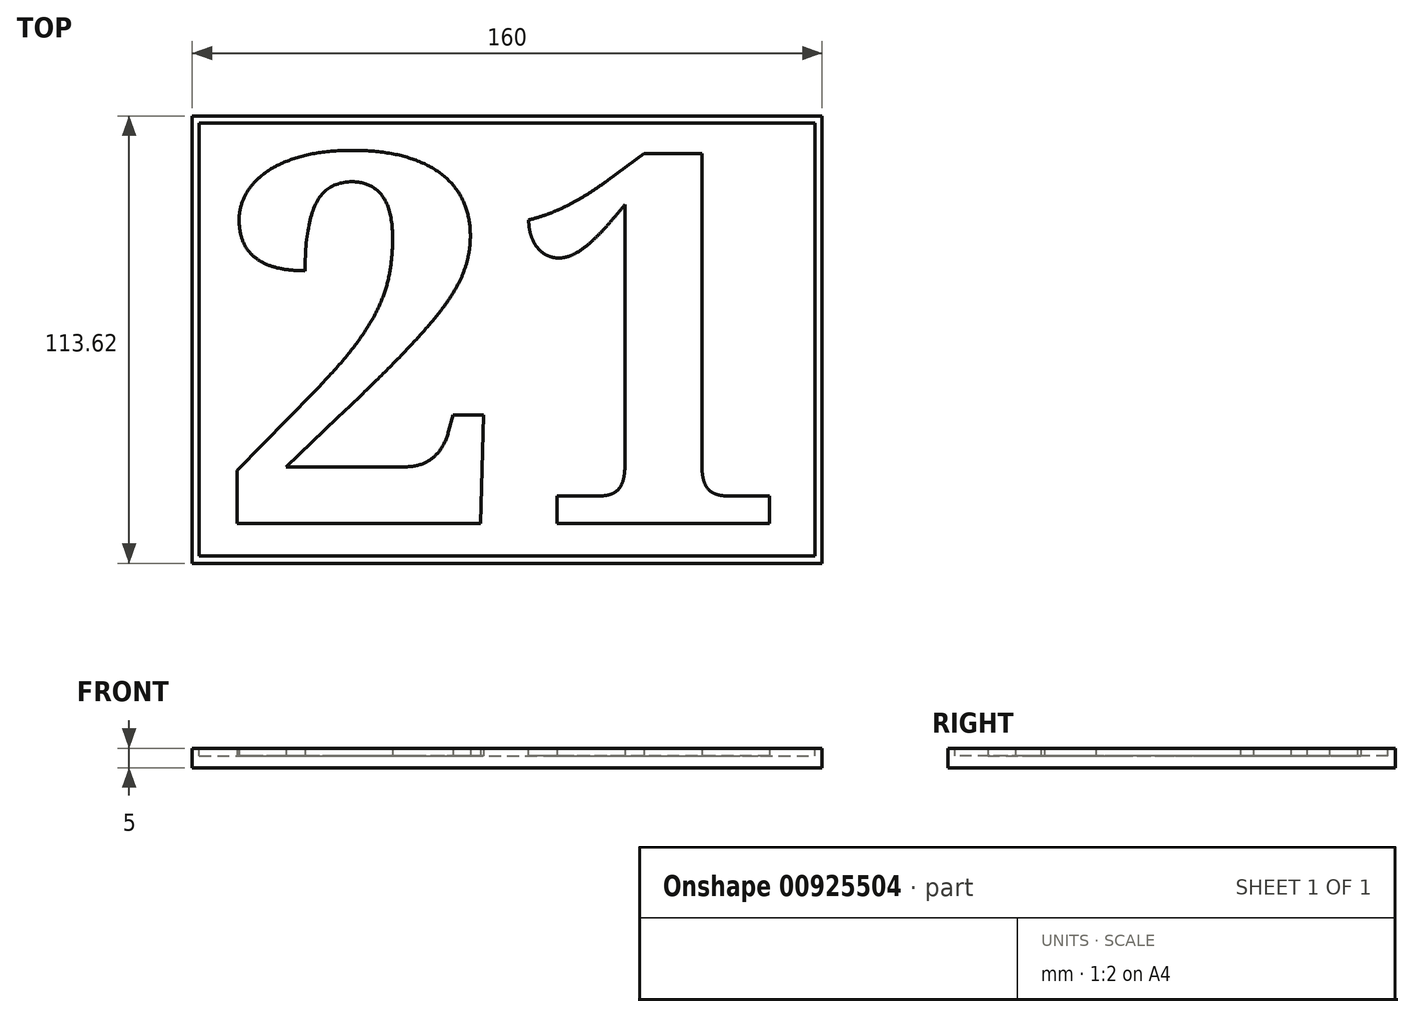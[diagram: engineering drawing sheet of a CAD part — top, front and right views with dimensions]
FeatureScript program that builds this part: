
annotation { "Feature Type Name" : "Feature", "Feature Type Description" : "" }
export const myFeature = defineFeature(function(context is Context, id is Id, definition is map)
    precondition{}
    {
        {
            var Q0;
            Q0=qCreatedBy(makeId("Top.planeOp"),FACE);
            var sketch = newSketch(context, id + "F0", { "sketchPlane" : qUnion([Q0])});
            skLineSegment(sketch, "E0.bottom", {"start": v(-80.27, 56.63) * mm, "end": v(79.73, 56.63) * mm});
            skLineSegment(sketch, "E0.top", {"start": v(-80.27, -57) * mm, "end": v(79.73, -57) * mm});
            skLineSegment(sketch, "E0.left", {"start": v(-80.27, 56.63) * mm, "end": v(-80.27, -57) * mm});
            skLineSegment(sketch, "E0.right", {"start": v(79.73, 56.63) * mm, "end": v(79.73, -57) * mm});
            skSolve(sketch);
        }
        {
            var Q0;
            Q0 = qSketchRegion(id + "F0", true);
            extrude(context, id + "F1", {"entities" : qUnion([Q0]), "depth" : 5 * mm, "offsetDistance" : 25 * mm});
        }
        {
            var Q0;
            Q0=makeQuery(id+"F1.opExtrude","CAP_FACE",FACE,{"disambiguationData":[OSD([sQuery(id+"F0.wireOp",EDGE,"E0.bottom"),sQuery(id+"F0.wireOp",EDGE,"E0.top"),sQuery(id+"F0.wireOp",EDGE,"E0.left"),sQuery(id+"F0.wireOp",EDGE,"E0.right")])],"isStart":false});
            var sketch = newSketch(context, id + "F2", { "sketchPlane" : qUnion([Q0])});
            skLineSegment(sketch, "E1.bottom", {"start": v(-78.47, 54.83) * mm, "end": v(77.93, 54.83) * mm});
            skLineSegment(sketch, "E1.top", {"start": v(-78.47, -55.2) * mm, "end": v(77.93, -55.2) * mm});
            skLineSegment(sketch, "E1.left", {"start": v(-78.47, 54.83) * mm, "end": v(-78.47, -55.2) * mm});
            skLineSegment(sketch, "E1.right", {"start": v(77.93, 54.83) * mm, "end": v(77.93, -55.2) * mm});
            skSolve(sketch);
        }
        {
            var Q0;
            Q0 = qSketchRegion(id + "F2", true);
            extrude(context, id + "F3", {"entities" : qUnion([Q0]), "operationType" : NewBodyOperationType.REMOVE, "oppositeDirection" : true, "depth" : 2 * mm, "offsetDistance" : 25 * mm});
        }
        {
            var Q0;
            Q0=makeQuery(id+"F3.boolean.opBoolean","COPY",FACE,{"derivedFrom":makeQuery(id+"F3.opExtrude","CAP_FACE",FACE,{"disambiguationData":[OSD([sQuery(id+"F2.wireOp",EDGE,"E1.bottom"),sQuery(id+"F2.wireOp",EDGE,"E1.top"),sQuery(id+"F2.wireOp",EDGE,"E1.left"),sQuery(id+"F2.wireOp",EDGE,"E1.right")])],"isStart":false})});
            var sketch = newSketch(context, id + "F4", { "sketchPlane" : qUnion([Q0])});
            skText(sketch, "E2", { "text": "21", "fontName": "NotoSerif-Bold.ttf"});
            const initialGuessF4  = {"E2": [-0.07347, -0.04687, 1, 0, 0.09424]};
            skSetInitialGuess(sketch, initialGuessF4);
            skSolve(sketch);
        }
        {
            var Q0;
            Q0 = qSketchRegion(id + "F4", true);
            extrude(context, id + "F5", {"entities" : qUnion([Q0]), "operationType" : NewBodyOperationType.ADD, "depth" : 2 * mm, "offsetDistance" : 25 * mm});
        }
    });
